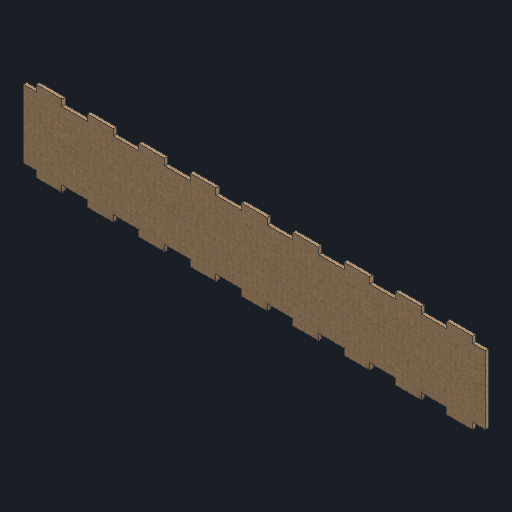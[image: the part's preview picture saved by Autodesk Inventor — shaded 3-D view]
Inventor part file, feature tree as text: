
AUTODESK INVENTOR PART (.ipt)
format: ipt  version: 2024.1 (Build 281209000, 209)  size: 253,440 bytes
history: native  units: in
note: dims shown in document units (in); Inventor stores cm internally (conversion verified against a paired STEP export)
features: other x4, reference x2, extrude x1, sketch x1
ambient origin geometry x8: Origin, YZ Plane, XZ Plane, XY Plane, X Axis, Y Axis, Z Axis, Center Point
bodies: Solid1 (feature_tree)
feature tree (8):
  extrude  "Extrusion1"  Depth=0.25in
  sketch  "Sketch1"  dims[d0=1.0in d1=0.25in d2=1.0in d3=0.25in d4=3.5433in d6=2.0in d7=0.3937in d9=1.0in d11=0.5in d12=0.5in d13=0.125in d14=0.0in]
  reference  "Reference1"
  reference  "Reference2"
  other  "<userpath>\Documents\School\FallCAD\Trebuchet\Trebuchet.iam"
  other  "Trebuchet.iam"
  other  "MainArm:1"
  other  "MainArm:2"
